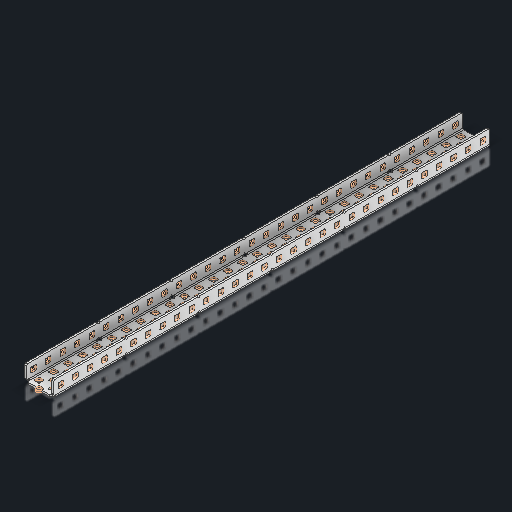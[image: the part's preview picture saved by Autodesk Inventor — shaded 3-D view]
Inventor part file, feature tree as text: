
AUTODESK INVENTOR PART (.ipt)
format: ipt  version: 2023.2 (Build 272271030, 271C)  size: 2,491,904 bytes
history: native  units: in
note: dims shown in document units (in); Inventor stores cm internally (conversion verified against a paired STEP export)
features: other x306, sketch x10, sheet_metal_op x1
ambient origin geometry x8: Origin, YZ Plane, XZ Plane, XY Plane, X Axis, Y Axis, Z Axis, Center Point
bodies: Solid1 (feature_tree)
feature tree (317):
  other  "Alu C 1x2x1x30.ipt"
  other  "Solid1::Alu C 1x2x1x30.ipt"
  other  "TaggingFeature1"
  sketch  "Sketch1"  dims[d0=0.3937in]
  sketch  "Sketch2"  dims[d1=0.0625in]
  sketch  "Sketch3"
  sketch  "Sketch7"
  other  "Flange Pattern Sketch"
  sketch  "Sketch8"
  sketch  "Sketch9"
  sheet_metal_op  "Body Pattern Sketch"
  sketch  "Sketch15"
  sketch  "Sketch16"
  other  "Arc Length"
  sketch  "Sketch13"
  sketch  "Sketch14"
  other  "Flange Pattern Plane"
  other  "Srf1"
  other  "Srf2"
  other  "Srf3"
  other  "Srf4"
  other  "Srf5"
  other  "Srf6"
  other  "Srf7"
  other  "Srf8"
  other  "Srf9"
  other  "Srf10"
  other  "Srf11"
  other  "Srf12"
  other  "Srf13"
  other  "Srf14"
  other  "Srf15"
  other  "Srf16"
  other  "Srf17"
  other  "Srf18"
  other  "Srf19"
  other  "Srf20"
  other  "Srf21"
  other  "Srf22"
  other  "Srf23"
  other  "Srf24"
  other  "Srf25"
  other  "Srf26"
  other  "Srf27"
  other  "Srf28"
  other  "Srf29"
  other  "Srf30"
  other  "Srf31"
  other  "Srf32"
  other  "Srf33"
  other  "Srf34"
  other  "Srf35"
  other  "Srf36"
  other  "Srf37"
  other  "Srf38"
  other  "Srf39"
  other  "Srf40"
  other  "Srf41"
  other  "Srf42"
  other  "Srf43"
  other  "Srf44"
  other  "Srf45"
  other  "Srf46"
  other  "Srf47"
  other  "Srf48"
  other  "Srf49"
  other  "Srf50"
  other  "Srf51"
  other  "Srf52"
  other  "Srf53"
  other  "Srf54"
  other  "Srf55"
  other  "Srf56"
  other  "Srf57"
  other  "Srf58"
  other  "Srf59"
  other  "Srf60"
  other  "Srf61"
  other  "Srf62"
  other  "Srf63"
  other  "Srf64"
  other  "Srf65"
  other  "Srf66"
  other  "Srf67"
  other  "Srf68"
  other  "Srf69"
  other  "Srf70"
  other  "Srf71"
  other  "Srf72"
  other  "Srf73"
  other  "Srf74"
  other  "Srf75"
  other  "Srf76"
  other  "Srf77"
  other  "Srf78"
  other  "Srf79"
  other  "Srf80"
  other  "Srf81"
  other  "Srf82"
  other  "Srf83"
  other  "Srf84"
  other  "Srf85"
  other  "Srf86"
  other  "Srf87"
  other  "Srf88"
  other  "Srf89"
  other  "Srf90"
  other  "Srf91"
  other  "Srf92"
  other  "Srf93"
  other  "Srf94"
  other  "Srf95"
  other  "Srf96"
  other  "Srf97"
  other  "Srf98"
  other  "Srf99"
  other  "Srf100"
  other  "Srf101"
  other  "Srf102"
  other  "Srf103"
  other  "Srf104"
  other  "Srf105"
  other  "Srf106"
  other  "Srf107"
  other  "Srf108"
  other  "Srf109"
  other  "Srf110"
  other  "Srf111"
  other  "Srf112"
  other  "Srf113"
  other  "Srf114"
  other  "Srf115"
  other  "Srf116"
  other  "Srf117"
  other  "Srf118"
  other  "Srf119"
  other  "Srf120"
  other  "Srf121"
  other  "Srf122"
  other  "Srf123"
  other  "Srf124"
  other  "Srf125"
  other  "Srf126"
  other  "Srf127"
  other  "Srf128"
  other  "Srf129"
  other  "Srf130"
  other  "Srf131"
  other  "Srf132"
  other  "Srf133"
  other  "Srf134"
  other  "Srf135"
  other  "Srf136"
  other  "Srf137"
  other  "Srf138"
  other  "Srf139"
  other  "Srf140"
  other  "Srf141"
  other  "Srf142"
  other  "Srf143"
  other  "Srf144"
  other  "Srf145"
  other  "Srf146"
  other  "Srf147"
  other  "Srf148"
  other  "Srf149"
  other  "Srf150"
  other  "Srf1::Derived"
  other  "Srf2::Derived"
  other  "Srf823::Derived"
  other  "Srf824::Derived"
  other  "Srf825::Derived"
  other  "Srf826::Derived"
  other  "Srf827::Derived"
  other  "Srf828::Derived"
  other  "Srf829::Derived"
  other  "Srf922::Derived"
  other  "Srf923::Derived"
  other  "Srf924::Derived"
  other  "Srf925::Derived"
  other  "Srf926::Derived"
  other  "Srf1143::Derived"
  other  "Srf1144::Derived"
  other  "Srf1145::Derived"
  other  "Srf1146::Derived"
  other  "Srf1147::Derived"
  other  "Srf1148::Derived"
  other  "Srf1149::Derived"
  other  "Srf1150::Derived"
  other  "Srf1151::Derived"
  other  "Srf1152::Derived"
  other  "Srf1153::Derived"
  other  "Srf1154::Derived"
  other  "Srf1155::Derived"
  other  "Srf1156::Derived"
  other  "Srf1157::Derived"
  other  "Srf1158::Derived"
  other  "Srf1159::Derived"
  other  "Srf1160::Derived"
  other  "Srf1161::Derived"
  other  "Srf1162::Derived"
  other  "Srf1163::Derived"
  other  "Srf1164::Derived"
  other  "Srf1165::Derived"
  other  "Srf1166::Derived"
  other  "Srf1167::Derived"
  other  "Srf1168::Derived"
  other  "Srf1169::Derived"
  other  "Srf1170::Derived"
  other  "Srf1171::Derived"
  other  "Srf1172::Derived"
  other  "Srf1173::Derived"
  other  "Srf1174::Derived"
  other  "Srf1175::Derived"
  other  "Srf1176::Derived"
  other  "Srf1177::Derived"
  other  "Srf1178::Derived"
  other  "Srf1179::Derived"
  other  "Srf1180::Derived"
  other  "Srf1181::Derived"
  other  "Srf1182::Derived"
  other  "Srf1183::Derived"
  other  "Srf1184::Derived"
  other  "Srf1185::Derived"
  other  "Srf1186::Derived"
  other  "Srf1187::Derived"
  other  "Srf1188::Derived"
  other  "Srf91::Derived"
  other  "Srf92::Derived"
  other  "Srf856::Derived"
  other  "Srf857::Derived"
  other  "Srf858::Derived"
  other  "Srf859::Derived"
  other  "Srf860::Derived"
  other  "Srf861::Derived"
  other  "Srf862::Derived"
  other  "Srf959::Derived"
  other  "Srf960::Derived"
  other  "Srf961::Derived"
  other  "Srf962::Derived"
  other  "Srf963::Derived"
  other  "Srf1199::Derived"
  other  "Srf1200::Derived"
  other  "Srf1201::Derived"
  other  "Srf1202::Derived"
  other  "Srf1203::Derived"
  other  "Srf1204::Derived"
  other  "Srf1205::Derived"
  other  "Srf1206::Derived"
  other  "Srf1207::Derived"
  other  "Srf1208::Derived"
  other  "Srf1209::Derived"
  other  "Srf1210::Derived"
  other  "Srf1211::Derived"
  other  "Srf1212::Derived"
  other  "Srf1213::Derived"
  other  "Srf1214::Derived"
  other  "Srf1215::Derived"
  other  "Srf1216::Derived"
  other  "Srf1217::Derived"
  other  "Srf1218::Derived"
  other  "Srf1219::Derived"
  other  "Srf1220::Derived"
  other  "Srf1221::Derived"
  other  "Srf1222::Derived"
  other  "Srf1223::Derived"
  other  "Srf1224::Derived"
  other  "Srf1225::Derived"
  other  "Srf1226::Derived"
  other  "Srf1227::Derived"
  other  "Srf1228::Derived"
  other  "Srf1229::Derived"
  other  "Srf1230::Derived"
  other  "Srf1231::Derived"
  other  "Srf1232::Derived"
  other  "Srf1233::Derived"
  other  "Srf1234::Derived"
  other  "Srf1235::Derived"
  other  "Srf1236::Derived"
  other  "Srf1237::Derived"
  other  "Srf1238::Derived"
  other  "Srf1239::Derived"
  other  "Srf1240::Derived"
  other  "Srf1241::Derived"
  other  "Srf1242::Derived"
  other  "Srf1243::Derived"
  other  "Srf1244::Derived"
  other  "Srf786::Derived"
  other  "Srf889::Derived"
  other  "Srf890::Derived"
  other  "Srf891::Derived"
  other  "Srf892::Derived"
  other  "Srf893::Derived"
  other  "Srf894::Derived"
  other  "Srf895::Derived"
  other  "Srf896::Derived"
  other  "Srf996::Derived"
  other  "Srf997::Derived"
  other  "Srf998::Derived"
  other  "Srf999::Derived"
  other  "Srf1000::Derived"
  other  "Srf1255::Derived"
  other  "Srf1256::Derived"
  other  "Srf1257::Derived"
  other  "Srf1258::Derived"
  other  "Srf1259::Derived"
  other  "Srf1260::Derived"
  other  "Srf1261::Derived"
  other  "Srf1262::Derived"
  other  "Srf1263::Derived"
  other  "Srf1264::Derived"
  other  "Srf1265::Derived"
  other  "Srf1266::Derived"
  other  "Srf1267::Derived"
  other  "Srf1268::Derived"
  other  "Srf1269::Derived"
  other  "Srf1270::Derived"
